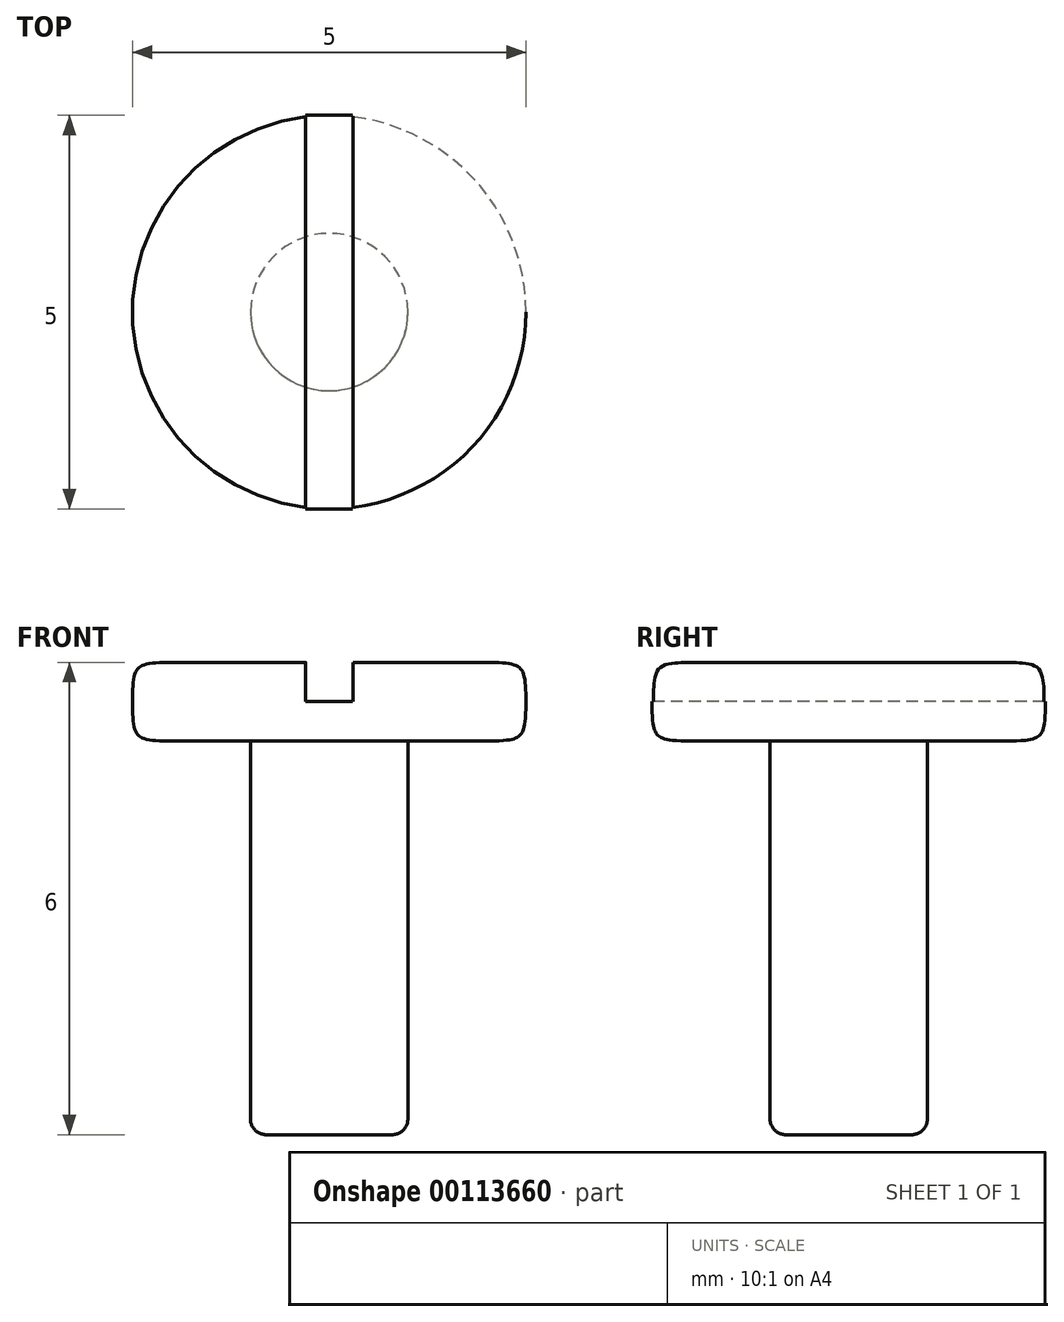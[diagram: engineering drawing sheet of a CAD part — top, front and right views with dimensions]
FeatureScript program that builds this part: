
annotation { "Feature Type Name" : "Feature", "Feature Type Description" : "" }
export const myFeature = defineFeature(function(context is Context, id is Id, definition is map)
    precondition{}
    {
        {
            var Q0;
            Q0=qCreatedBy(makeId("Top.planeOp"),FACE);
            var sketch = newSketch(context, id + "F0", { "sketchPlane" : qUnion([Q0])});
            skCircle(sketch, "E0", {"center": v(0, 0) * mm, "radius": 2.5 * mm});
            skSolve(sketch);
        }
        {
            var Q0;
            Q0=makeQuery(id+"F0.imprint","IMPRINT",FACE,{"disambiguationData":[TD([[makeQuery(id+"F0.imprint","IMPRINT",EDGE,{"derivedFrom":sQuery(id+"F0.wireOp",EDGE,"E0")}),1.0]])]});
            extrude(context, id + "F1", {"entities" : qUnion([Q0]), "oppositeDirection" : true, "depth" : 1 * mm});
        }
        {
            var Q0;
            Q0=makeQuery(id+"F1.opExtrude","CAP_EDGE",EDGE,{"disambiguationData":[OSD([sQuery(id+"F0.wireOp",EDGE,"E0")])],"isStart":true});
            var Q1;
            Q1=makeQuery(id+"F1.opExtrude","CAP_EDGE",EDGE,{"disambiguationData":[OSD([sQuery(id+"F0.wireOp",EDGE,"E0")])],"isStart":false});
            fillet(context, id + "F2", {"entities" : qUnion([Q0, Q1]), "radius" : 0.5 * mm, "tangentPropagation" : true, "rho" : 0.7, "crossSection" : FilletCrossSection.CONIC, "allowEdgeOverflow" : false});
        }
        {
            var Q0;
            Q0=makeQuery(id+"F1.opExtrude","CAP_FACE",FACE,{"disambiguationData":[OSD([sQuery(id+"F0.wireOp",EDGE,"E0")])],"isStart":false});
            var sketch = newSketch(context, id + "F3", { "sketchPlane" : qUnion([Q0])});
            skCircle(sketch, "E1", {"center": v(0, 0) * mm, "radius": 1 * mm});
            skSolve(sketch);
        }
        {
            var Q0;
            Q0=makeQuery(id+"F3.imprint","IMPRINT",FACE,{"disambiguationData":[TD([[makeQuery(id+"F3.imprint","IMPRINT",EDGE,{"derivedFrom":sQuery(id+"F3.wireOp",EDGE,"E1")}),1.0]])]});
            extrude(context, id + "F4", {"entities" : qUnion([Q0]), "operationType" : NewBodyOperationType.ADD, "depth" : 5 * mm});
        }
        {
            var Q0;
            Q0=makeQuery(id+"F4.opExtrude","CAP_EDGE",EDGE,{"disambiguationData":[OSD([sQuery(id+"F3.wireOp",EDGE,"E1")])],"isStart":true});
            var Q1;
            Q1=makeQuery(id+"F4.opExtrude","CAP_EDGE",EDGE,{"disambiguationData":[OSD([sQuery(id+"F3.wireOp",EDGE,"E1")])],"isStart":false});
            fillet(context, id + "F5", {"entities" : qUnion([Q0, Q1]), "radius" : 0.2 * mm, "tangentPropagation" : true, "allowEdgeOverflow" : false});
        }
        {
            var Q0;
            Q0=qCreatedBy(makeId("Top.planeOp"),FACE);
            var sketch = newSketch(context, id + "F6", { "sketchPlane" : qUnion([Q0])});
            skLineSegment(sketch, "E2.bottom", {"start": v(0.3, 2.5) * mm, "end": v(-0.3, 2.5) * mm});
            skLineSegment(sketch, "E2.top", {"start": v(0.3, -2.5) * mm, "end": v(-0.3, -2.5) * mm});
            skLineSegment(sketch, "E2.left", {"start": v(0.3, 2.5) * mm, "end": v(0.3, -2.5) * mm});
            skLineSegment(sketch, "E2.right", {"start": v(-0.3, 2.5) * mm, "end": v(-0.3, -2.5) * mm});
            skPoint(sketch, "E2.middle", {"position": v(0, 0) * mm});
            skSolve(sketch);
        }
        {
            var Q0;
            {var subQ0=sQuery(id+"F6.wireOp",EDGE,"E2.left");var subQ1=sQuery(id+"F0.wireOp",EDGE,"E0");var subQ2=makeQuery(id+"F2.opFillet","BLEND_EDGE",EDGE,{"blendedFrom":[makeQuery(id+"F1.opExtrude","CAP_EDGE",EDGE,{"disambiguationData":[OSD([subQ1])],"isStart":true}),makeQuery(id+"F1.opExtrude","CAP_FACE",FACE,{"disambiguationData":[OSD([subQ1])],"isStart":true})],"blendedInto":[makeQuery(id+"F1.opExtrude","CAP_FACE",FACE,{"disambiguationData":[OSD([subQ1])],"isStart":true})]});var subQ3=makeQuery(id+"F6.imprint","INTERSECT",VERTEX,{"disambiguationData":[OD(0.0)],"derivedFrom":[subQ2,subQ0]});Q0=makeQuery(id+"F6.imprint","IMPRINT",FACE,{"disambiguationData":[TD([[makeQuery(id+"F6.imprint","IMPRINT",EDGE,{"disambiguationData":[TD([[subQ3,-1.0]])],"derivedFrom":subQ0}),-1.0]])]});}
            extrude(context, id + "F7", {"entities" : qUnion([Q0]), "operationType" : NewBodyOperationType.REMOVE, "oppositeDirection" : true, "depth" : 0.5 * mm});
        }
    });
